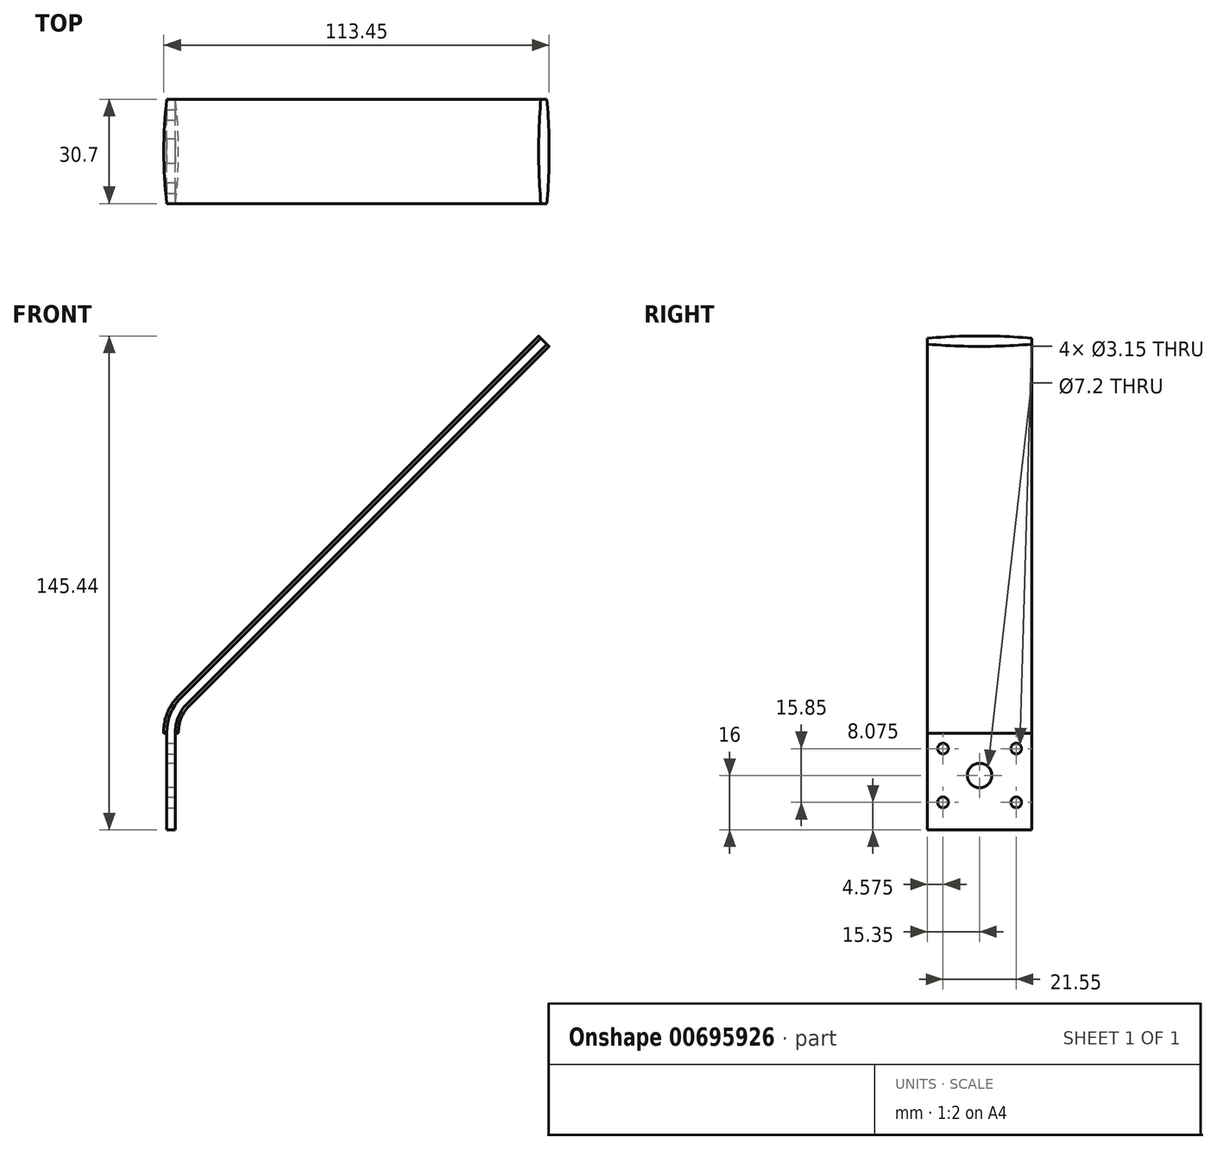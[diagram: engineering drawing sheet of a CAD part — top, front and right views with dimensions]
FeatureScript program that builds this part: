
annotation { "Feature Type Name" : "Feature", "Feature Type Description" : "" }
export const myFeature = defineFeature(function(context is Context, id is Id, definition is map)
    precondition{}
    {
        {
            var Q0;
            Q0=qCreatedBy(makeId("Front.planeOp"),FACE);
            var sketch = newSketch(context, id + "F0", { "sketchPlane" : qUnion([Q0])});
            skLineSegment(sketch, "E0", {"start": v(0, 0) * mm, "end": v(0, 29) * mm});
            skArc(sketch, "E1", {"start": v(3.66, 37.84) * mm, "mid": v(0.95, 33.78) * mm, "end": v(0, 29) * mm});
            skLineSegment(sketch, "E2", {"start": v(3.66, 37.84) * mm, "end": v(109.73, 143.9) * mm});
            skSolve(sketch);
        }
        {
            var Q0;
            Q0=qCreatedBy(makeId("Top.planeOp"),FACE);
            var sketch = newSketch(context, id + "F1", { "sketchPlane" : qUnion([Q0])});
            skLineSegment(sketch, "E3", {"start": v(-1.25, -15.35) * mm, "end": v(1.25, -15.35) * mm});
            skLineSegment(sketch, "E4", {"start": v(-1.25, 15.35) * mm, "end": v(1.25, 15.35) * mm});
            skArc(sketch, "E5", {"start": v(-1.25, 15.35) * mm, "mid": v(-2.17, 0) * mm, "end": v(-1.25, -15.35) * mm});
            skArc(sketch, "E6", {"start": v(1.25, -15.35) * mm, "mid": v(2.17, 0) * mm, "end": v(1.25, 15.35) * mm});
            skPoint(sketch, "E7", {"position": v(0, 15.35) * mm});
            skLineSegment(sketch, "E8", {"start": v(0, 15.35) * mm, "end": v(0, -15.35) * mm, "construction": true});
            skLineSegment(sketch, "E9", {"start": v(-2.18, 0) * mm, "end": v(2.18, 0) * mm, "construction": true});
            skSolve(sketch);
        }
        {
            var Q0;
            Q0 = qSketchRegion(id + "F1", true);
            var Q1;
            Q1 = qConstructionFilter(qBodyType(qCreatedBy(id + "F0" ,EDGE), BodyType.WIRE), ConstructionObject.NO);
            sweep(context, id + "F2", {"profiles" : qUnion([Q0]), "path" : qUnion([Q1])});
        }
        {
            var Q0;
            Q0=makeQuery(id+"F2.opSweep","CAP_FACE",FACE,{"disambiguationData":[OSD([sQuery(id+"F0.wireOp",VERTEX,"E0.start"),sQuery(id+"F1.wireOp",EDGE,"E3"),sQuery(id+"F1.wireOp",EDGE,"E4"),sQuery(id+"F1.wireOp",EDGE,"E5"),sQuery(id+"F1.wireOp",EDGE,"E6")])],"isStart":true});
            var sketch = newSketch(context, id + "F3", { "sketchPlane" : qUnion([Q0])});
            skLineSegment(sketch, "E10.bottom", {"start": v(-1.25, 15.35) * mm, "end": v(-6.68, 15.35) * mm});
            skLineSegment(sketch, "E10.top", {"start": v(-1.25, -15.35) * mm, "end": v(-6.68, -15.35) * mm});
            skLineSegment(sketch, "E10.left", {"start": v(-1.25, 15.35) * mm, "end": v(-1.25, -15.35) * mm});
            skLineSegment(sketch, "E10.right", {"start": v(-6.68, 15.35) * mm, "end": v(-6.68, -15.35) * mm});
            skLineSegment(sketch, "E11.bottom", {"start": v(1.25, 15.35) * mm, "end": v(4.39, 15.35) * mm});
            skLineSegment(sketch, "E11.top", {"start": v(1.25, -15.35) * mm, "end": v(4.39, -15.35) * mm});
            skLineSegment(sketch, "E11.left", {"start": v(1.25, 15.35) * mm, "end": v(1.25, -15.35) * mm});
            skLineSegment(sketch, "E11.right", {"start": v(4.39, 15.35) * mm, "end": v(4.39, -15.35) * mm});
            skSolve(sketch);
        }
        {
            var Q0;
            Q0 = qSketchRegion(id + "F3", true);
            extrude(context, id + "F4", {"entities" : qUnion([Q0]), "operationType" : NewBodyOperationType.REMOVE, "oppositeDirection" : true, "depth" : 28.5 * mm, "offsetDistance" : 25 * mm});
        }
        {
            var Q0;
            Q0=qCreatedBy(makeId("Right.planeOp"),FACE);
            var sketch = newSketch(context, id + "F5", { "sketchPlane" : qUnion([Q0])});
            skCircle(sketch, "E12", {"center": v(0, 16) * mm, "radius": 3.6 * mm});
            skSolve(sketch);
        }
        {
            var Q0;
            Q0 = qSketchRegion(id + "F5", true);
            extrude(context, id + "F6", {"entities" : qUnion([Q0]), "operationType" : NewBodyOperationType.REMOVE, "endBound" : BoundingType.THROUGH_ALL, "depth" : 25 * mm, "offsetDistance" : 25 * mm, "hasSecondDirection" : true, "secondDirectionBound" : SecondDirectionBoundingType.THROUGH_ALL, "secondDirectionOppositeDirection" : true, "secondDirectionDepth" : 25 * mm});
        }
        {
            var Q0;
            Q0=qCreatedBy(makeId("Right.planeOp"),FACE);
            var sketch = newSketch(context, id + "F7", { "sketchPlane" : qUnion([Q0])});
            skCircle(sketch, "E13", {"center": v(-10.78, 23.93) * mm, "radius": 1.57 * mm});
            skLineSegment(sketch, "E14", {"start": v(0, 0) * mm, "end": v(0, 28.97) * mm, "construction": true});
            skLineSegment(sketch, "E15", {"start": v(16.08, 16) * mm, "end": v(-14.57, 16) * mm, "construction": true});
            skLineSegment(sketch, "E16", {"start": v(-3.6, 16) * mm, "end": v(3.6, 16) * mm, "construction": true});
            skLineSegment(sketch, "E17", {"start": v(0, 19.6) * mm, "end": v(0, 12.4) * mm, "construction": true});
            skPoint(sketch, "E18", {"position": v(0, 16) * mm});
            skCircle(sketch, "E19.MirrorC", {"center": v(10.78, 23.93) * mm, "radius": 1.57 * mm});
            skCircle(sketch, "E20.MirrorC", {"center": v(10.78, 8.08) * mm, "radius": 1.57 * mm});
            skCircle(sketch, "E21.MirrorC", {"center": v(-10.78, 8.08) * mm, "radius": 1.57 * mm});
            skSolve(sketch);
        }
        {
            var Q0;
            Q0 = qSketchRegion(id + "F7", true);
            extrude(context, id + "F8", {"entities" : qUnion([Q0]), "operationType" : NewBodyOperationType.REMOVE, "endBound" : BoundingType.THROUGH_ALL, "oppositeDirection" : true, "depth" : 25 * mm, "offsetDistance" : 25 * mm, "hasSecondDirection" : true, "secondDirectionBound" : SecondDirectionBoundingType.THROUGH_ALL, "secondDirectionOppositeDirection" : false, "secondDirectionDepth" : 25 * mm});
        }
    });
